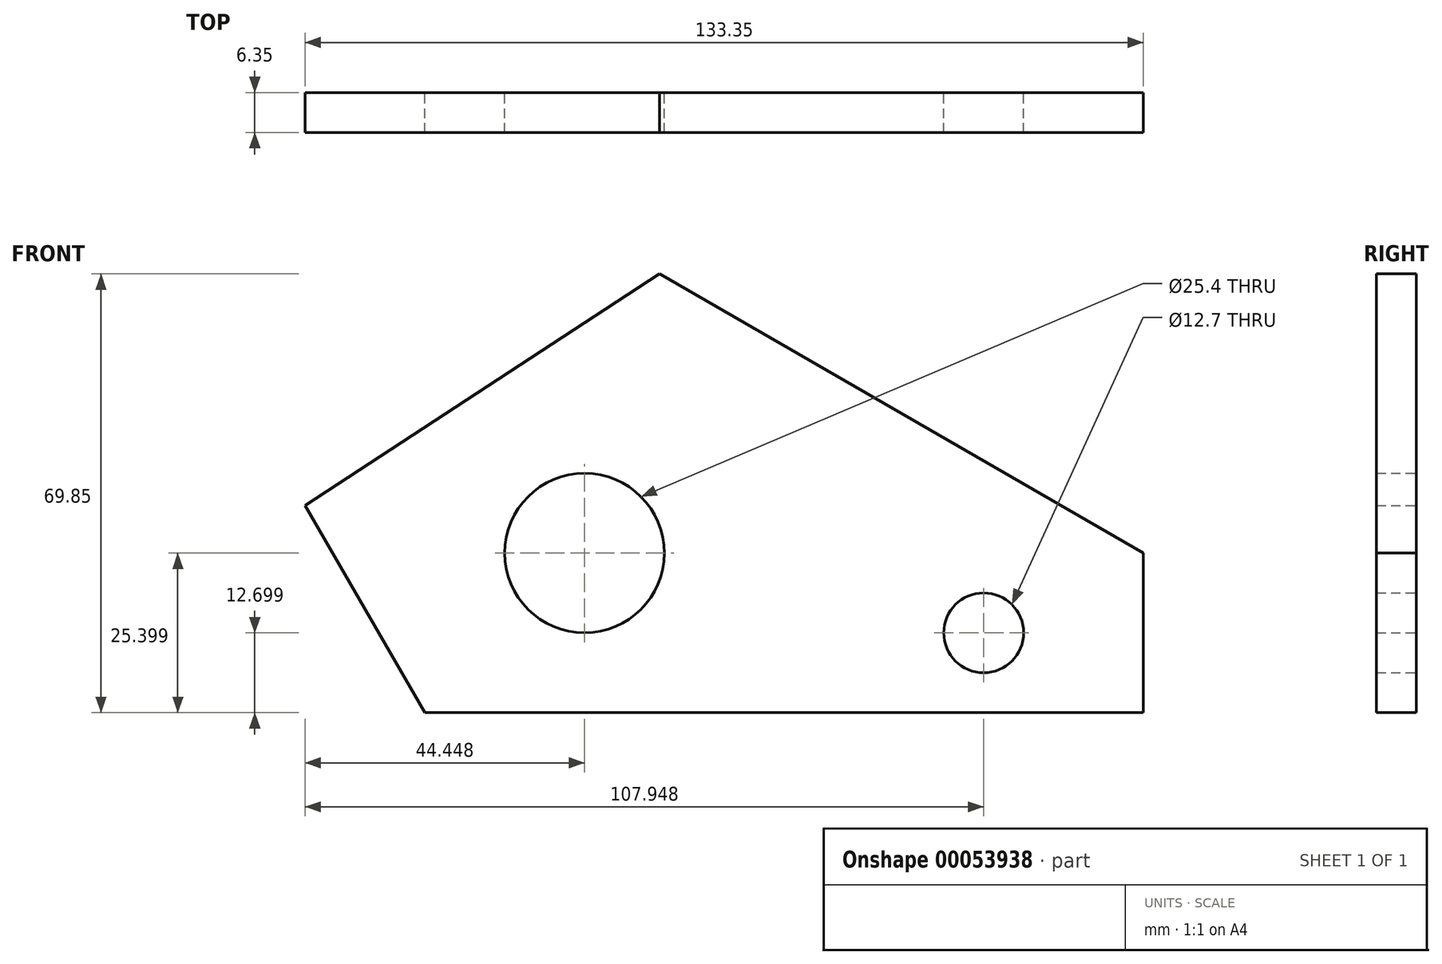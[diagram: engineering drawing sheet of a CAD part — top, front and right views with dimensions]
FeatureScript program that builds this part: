
annotation { "Feature Type Name" : "Feature", "Feature Type Description" : "" }
export const myFeature = defineFeature(function(context is Context, id is Id, definition is map)
    precondition{}
    {
        {
            var Q0;
            Q0=qCreatedBy(makeId("Front.planeOp"),FACE);
            var sketch = newSketch(context, id + "F0", { "sketchPlane" : qUnion([Q0])});
            skLineSegment(sketch, "E0", {"start": v(-98.63, 22.43) * mm, "end": v(-79.58, -10.56) * mm});
            skLineSegment(sketch, "E1", {"start": v(-79.58, -10.56) * mm, "end": v(34.72, -10.56) * mm});
            skLineSegment(sketch, "E2", {"start": v(34.72, -10.56) * mm, "end": v(34.72, 14.84) * mm});
            skLineSegment(sketch, "E3", {"start": v(34.72, 14.84) * mm, "end": v(-42.27, 59.29) * mm});
            skLineSegment(sketch, "E4", {"start": v(-42.27, 59.29) * mm, "end": v(-98.63, 22.43) * mm});
            skCircle(sketch, "E5", {"center": v(-54.18, 14.84) * mm, "radius": 12.7 * mm});
            skCircle(sketch, "E6", {"center": v(9.32, 2.14) * mm, "radius": 6.35 * mm});
            skSolve(sketch);
        }
        {
            var Q0;
            Q0 = qSketchRegion(id + "F0", true);
            extrude(context, id + "F1", {"entities" : qUnion([Q0]), "depth" : 6.35 * mm});
        }
    });
